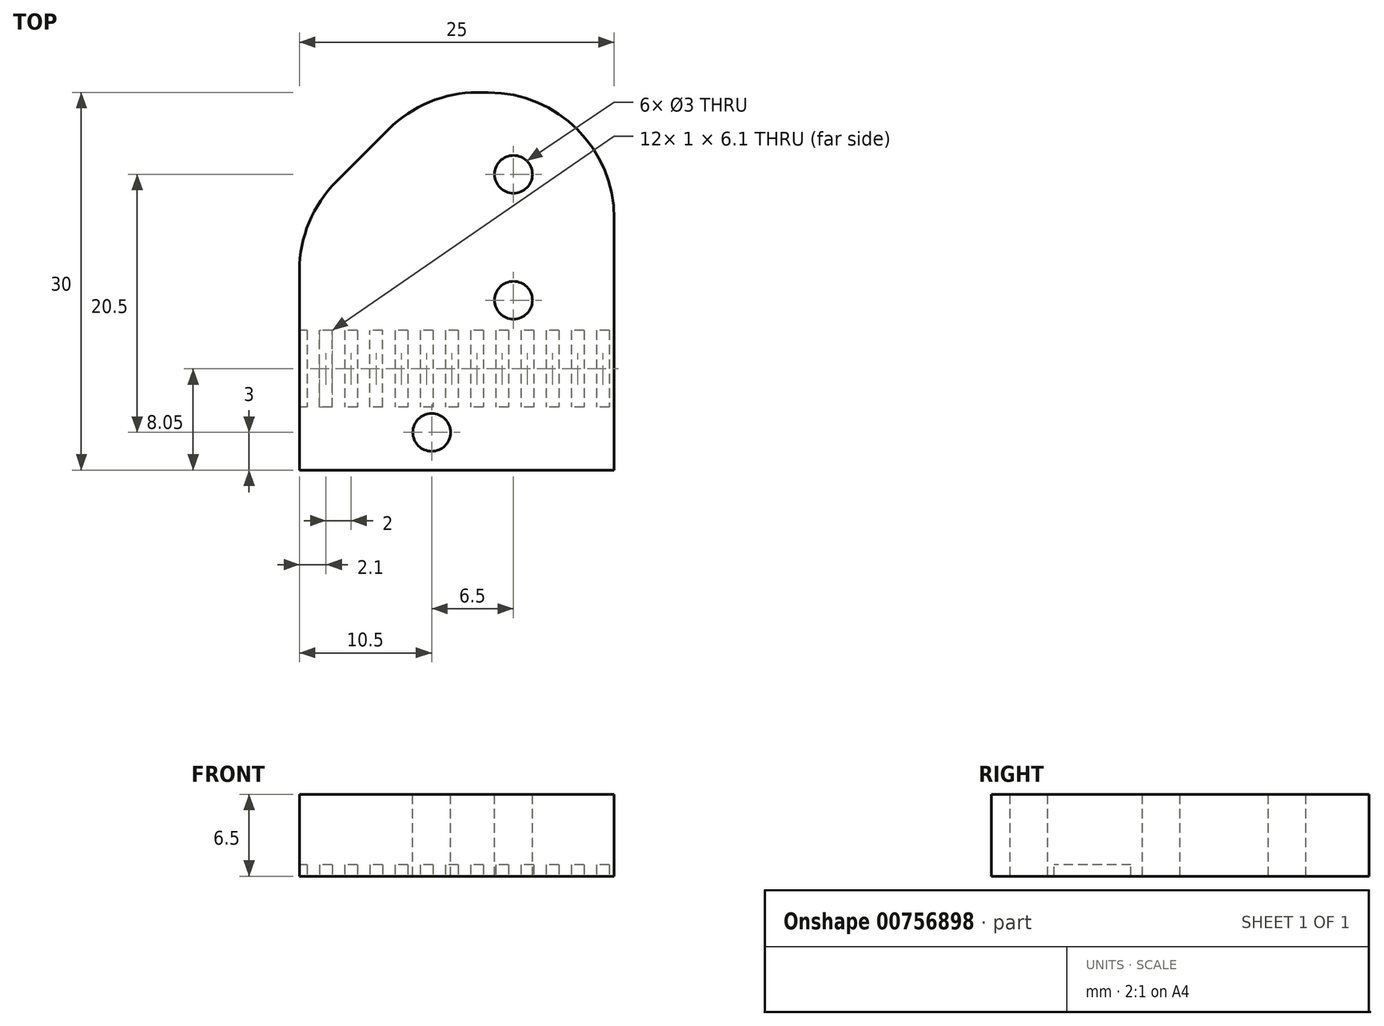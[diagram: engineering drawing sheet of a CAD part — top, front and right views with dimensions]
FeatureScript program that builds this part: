
annotation { "Feature Type Name" : "Feature", "Feature Type Description" : "" }
export const myFeature = defineFeature(function(context is Context, id is Id, definition is map)
    precondition{}
    {
        {
            var Q0;
            Q0=qCreatedBy(makeId("Top.planeOp"),FACE);
            var sketch = newSketch(context, id + "F0", { "sketchPlane" : qUnion([Q0])});
            skLineSegment(sketch, "E0.bottom", {"start": v(12.5, -15) * mm, "end": v(-12.5, -15) * mm});
            skLineSegment(sketch, "E0.top", {"start": v(12.5, 15) * mm, "end": v(-12.5, 15) * mm});
            skLineSegment(sketch, "E0.left", {"start": v(12.5, -15) * mm, "end": v(12.5, 15) * mm});
            skLineSegment(sketch, "E0.right", {"start": v(-12.5, -15) * mm, "end": v(-12.5, 15) * mm});
            skPoint(sketch, "E0.middle", {"position": v(0, 0) * mm});
            skSolve(sketch);
        }
        {
            var Q0;
            Q0=makeQuery(id+"F0.imprint","IMPRINT",FACE,{"disambiguationData":[TD([[makeQuery(id+"F0.imprint","IMPRINT",EDGE,{"derivedFrom":sQuery(id+"F0.wireOp",EDGE,"E0.bottom")}),-1.0]])]});
            extrude(context, id + "F1", {"entities" : qUnion([Q0]), "depth" : 6.5 * mm, "offsetDistance" : 25 * mm});
        }
        {
            var Q0;
            Q0=makeQuery(id+"F1.opExtrude","CAP_FACE",FACE,{"disambiguationData":[OSD([sQuery(id+"F0.wireOp",EDGE,"E0.bottom"),sQuery(id+"F0.wireOp",EDGE,"E0.top"),sQuery(id+"F0.wireOp",EDGE,"E0.left"),sQuery(id+"F0.wireOp",EDGE,"E0.right")])],"isStart":false});
            var sketch = newSketch(context, id + "F2", { "sketchPlane" : qUnion([Q0])});
            skCircle(sketch, "E1", {"center": v(-2, -12) * mm, "radius": 1.5 * mm});
            skPoint(sketch, "E1.centerSnap0", {"position": v(0, -15) * mm});
            skCircle(sketch, "E2", {"center": v(4.5, -1.5) * mm, "radius": 1.5 * mm});
            skCircle(sketch, "E3", {"center": v(4.5, 8.5) * mm, "radius": 1.5 * mm});
            skSolve(sketch);
        }
        {
            var Q0;
            Q0=qSketchRegion(id+"F2",true);
            extrude(context, id + "F3", {"entities" : qUnion([Q0]), "operationType" : NewBodyOperationType.REMOVE, "endBound" : BoundingType.THROUGH_ALL, "oppositeDirection" : true, "depth" : 25 * mm, "offsetDistance" : 25 * mm});
        }
        {
            var Q0;
            {var subQ0=sQuery(id+"F0.wireOp",EDGE,"E0.right");var subQ1=sQuery(id+"F0.wireOp",EDGE,"E0.left");var subQ2=sQuery(id+"F0.wireOp",EDGE,"E0.top");Q0=makeQuery(id+"F5.boolean.opBoolean","SPLIT",FACE,{"disambiguationData":[TD([makeQuery(id+"F1.opExtrude","SWEPT_FACE",FACE,{"disambiguationData":[OSD([subQ2])]})])],"derivedFrom":makeQuery(id+"F1.opExtrude","CAP_FACE",FACE,{"disambiguationData":[OSD([sQuery(id+"F0.wireOp",EDGE,"E0.bottom"),subQ2,subQ1,subQ0])],"isStart":true})});}
            var sketch = newSketch(context, id + "F4", { "sketchPlane" : qUnion([Q0])});
            skLineSegment(sketch, "E4.bottom", {"start": v(12.1, 3.9) * mm, "end": v(11.1, 3.9) * mm});
            skLineSegment(sketch, "E4.top", {"start": v(12.1, 10) * mm, "end": v(11.1, 10) * mm});
            skLineSegment(sketch, "E4.left", {"start": v(12.1, 3.9) * mm, "end": v(12.1, 10) * mm});
            skLineSegment(sketch, "E4.right", {"start": v(11.1, 3.9) * mm, "end": v(11.1, 10) * mm});
            skPoint(sketch, "E4.middle", {"position": v(11.6, 6.95) * mm});
            skLineSegment(sketch, "E5.bottom", {"start": v(10.1, 3.9) * mm, "end": v(9.1, 3.9) * mm});
            skLineSegment(sketch, "E5.top", {"start": v(10.1, 10) * mm, "end": v(9.1, 10) * mm});
            skLineSegment(sketch, "E5.left", {"start": v(10.1, 3.9) * mm, "end": v(10.1, 10) * mm});
            skLineSegment(sketch, "E5.right", {"start": v(9.1, 3.9) * mm, "end": v(9.1, 10) * mm});
            skPoint(sketch, "E5.middle", {"position": v(9.6, 6.95) * mm});
            skLineSegment(sketch, "E6.bottom", {"start": v(8.1, 3.9) * mm, "end": v(7.1, 3.9) * mm});
            skLineSegment(sketch, "E6.top", {"start": v(8.1, 10) * mm, "end": v(7.1, 10) * mm});
            skLineSegment(sketch, "E6.left", {"start": v(8.1, 3.9) * mm, "end": v(8.1, 10) * mm});
            skLineSegment(sketch, "E6.right", {"start": v(7.1, 3.9) * mm, "end": v(7.1, 10) * mm});
            skPoint(sketch, "E6.middle", {"position": v(7.6, 6.95) * mm});
            skLineSegment(sketch, "E7.bottom", {"start": v(6.1, 3.9) * mm, "end": v(5.1, 3.9) * mm});
            skLineSegment(sketch, "E7.top", {"start": v(6.1, 10) * mm, "end": v(5.1, 10) * mm});
            skLineSegment(sketch, "E7.left", {"start": v(6.1, 3.9) * mm, "end": v(6.1, 10) * mm});
            skLineSegment(sketch, "E7.right", {"start": v(5.1, 3.9) * mm, "end": v(5.1, 10) * mm});
            skPoint(sketch, "E7.middle", {"position": v(5.6, 6.95) * mm});
            skLineSegment(sketch, "E8.bottom", {"start": v(4.1, 3.9) * mm, "end": v(3.1, 3.9) * mm});
            skLineSegment(sketch, "E8.top", {"start": v(4.1, 10) * mm, "end": v(3.1, 10) * mm});
            skLineSegment(sketch, "E8.left", {"start": v(4.1, 3.9) * mm, "end": v(4.1, 10) * mm});
            skLineSegment(sketch, "E8.right", {"start": v(3.1, 3.9) * mm, "end": v(3.1, 10) * mm});
            skPoint(sketch, "E8.middle", {"position": v(3.6, 6.95) * mm});
            skLineSegment(sketch, "E9.bottom", {"start": v(2.1, 3.9) * mm, "end": v(1.1, 3.9) * mm});
            skLineSegment(sketch, "E9.top", {"start": v(2.1, 10) * mm, "end": v(1.1, 10) * mm});
            skLineSegment(sketch, "E9.left", {"start": v(2.1, 3.9) * mm, "end": v(2.1, 10) * mm});
            skLineSegment(sketch, "E9.right", {"start": v(1.1, 3.9) * mm, "end": v(1.1, 10) * mm});
            skPoint(sketch, "E9.middle", {"position": v(1.6, 6.95) * mm});
            skLineSegment(sketch, "E10.bottom", {"start": v(0.1, 3.9) * mm, "end": v(-0.9, 3.9) * mm});
            skLineSegment(sketch, "E10.top", {"start": v(0.1, 10) * mm, "end": v(-0.9, 10) * mm});
            skLineSegment(sketch, "E10.left", {"start": v(0.1, 3.9) * mm, "end": v(0.1, 10) * mm});
            skLineSegment(sketch, "E10.right", {"start": v(-0.9, 3.9) * mm, "end": v(-0.9, 10) * mm});
            skPoint(sketch, "E10.middle", {"position": v(-0.4, 6.95) * mm});
            skLineSegment(sketch, "E11", {"start": v(-12.5, 3.9) * mm, "end": v(12.5, 3.9) * mm, "construction": true});
            skLineSegment(sketch, "E12", {"start": v(12.5, 10) * mm, "end": v(-12.5, 10) * mm, "construction": true});
            skLineSegment(sketch, "E13.bottom", {"start": v(-1.9, 3.9) * mm, "end": v(-2.9, 3.9) * mm});
            skLineSegment(sketch, "E13.top", {"start": v(-1.9, 10) * mm, "end": v(-2.9, 10) * mm});
            skLineSegment(sketch, "E13.left", {"start": v(-1.9, 3.9) * mm, "end": v(-1.9, 10) * mm});
            skLineSegment(sketch, "E13.right", {"start": v(-2.9, 3.9) * mm, "end": v(-2.9, 10) * mm});
            skLineSegment(sketch, "E14.bottom", {"start": v(-3.9, 3.9) * mm, "end": v(-4.9, 3.9) * mm});
            skLineSegment(sketch, "E14.top", {"start": v(-3.9, 10) * mm, "end": v(-4.9, 10) * mm});
            skLineSegment(sketch, "E14.left", {"start": v(-3.9, 3.9) * mm, "end": v(-3.9, 10) * mm});
            skLineSegment(sketch, "E14.right", {"start": v(-4.9, 3.9) * mm, "end": v(-4.9, 10) * mm});
            skLineSegment(sketch, "E15.bottom", {"start": v(-5.9, 10) * mm, "end": v(-6.9, 10) * mm});
            skLineSegment(sketch, "E15.top", {"start": v(-5.9, 3.9) * mm, "end": v(-6.9, 3.9) * mm});
            skLineSegment(sketch, "E15.left", {"start": v(-5.9, 10) * mm, "end": v(-5.9, 3.9) * mm});
            skLineSegment(sketch, "E15.right", {"start": v(-6.9, 10) * mm, "end": v(-6.9, 3.9) * mm});
            skLineSegment(sketch, "E16.bottom", {"start": v(-7.9, 3.9) * mm, "end": v(-8.9, 3.9) * mm});
            skLineSegment(sketch, "E16.top", {"start": v(-7.9, 10) * mm, "end": v(-8.9, 10) * mm});
            skLineSegment(sketch, "E16.left", {"start": v(-7.9, 3.9) * mm, "end": v(-7.9, 10) * mm});
            skLineSegment(sketch, "E16.right", {"start": v(-8.9, 3.9) * mm, "end": v(-8.9, 10) * mm});
            skLineSegment(sketch, "E17.bottom", {"start": v(-9.9, 10) * mm, "end": v(-10.9, 10) * mm});
            skLineSegment(sketch, "E17.top", {"start": v(-9.9, 3.9) * mm, "end": v(-10.9, 3.9) * mm});
            skLineSegment(sketch, "E17.left", {"start": v(-9.9, 10) * mm, "end": v(-9.9, 3.9) * mm});
            skLineSegment(sketch, "E17.right", {"start": v(-10.9, 10) * mm, "end": v(-10.9, 3.9) * mm});
            skLineSegment(sketch, "E18.bottom", {"start": v(-11.9, 3.9) * mm, "end": v(-12.9, 3.9) * mm});
            skLineSegment(sketch, "E18.top", {"start": v(-11.9, 10) * mm, "end": v(-12.9, 10) * mm});
            skLineSegment(sketch, "E18.left", {"start": v(-11.9, 3.9) * mm, "end": v(-11.9, 10) * mm});
            skLineSegment(sketch, "E18.right", {"start": v(-12.9, 3.9) * mm, "end": v(-12.9, 10) * mm});
            skSolve(sketch);
        }
        {
            var Q0;
            Q0 = qSketchRegion(id + "F4", true);
            extrude(context, id + "F5", {"entities" : qUnion([Q0]), "operationType" : NewBodyOperationType.REMOVE, "oppositeDirection" : true, "depth" : 0.9 * mm, "offsetDistance" : 25 * mm});
        }
        {
            var Q0;
            Q0=makeQuery(id+"F1.opExtrude","SWEPT_EDGE",EDGE,{"disambiguationData":[OSD([sQuery(id+"F0.wireOp",EDGE,"E0.top"),sQuery(id+"F0.wireOp",EDGE,"E0.right")])]});
            chamfer(context, id + "F6", {"entities" : qUnion([Q0]), "width" : 10 * mm, "tangentPropagation" : true});
        }
        {
            var Q0;
            {var subQ0=sQuery(id+"F0.wireOp",EDGE,"E0.right");Q0=makeQuery(id+"F6.opChamfer","BLEND_EDGE",EDGE,{"blendedFrom":[makeQuery(id+"F1.opExtrude","SWEPT_EDGE",EDGE,{"disambiguationData":[OSD([sQuery(id+"F0.wireOp",EDGE,"E0.top"),subQ0])]}),makeQuery(id+"F1.opExtrude","SWEPT_FACE",FACE,{"disambiguationData":[OSD([subQ0])]})],"blendedInto":[makeQuery(id+"F1.opExtrude","SWEPT_FACE",FACE,{"disambiguationData":[OSD([subQ0])]})]});}
            var Q1;
            {var subQ0=sQuery(id+"F0.wireOp",EDGE,"E0.top");Q1=makeQuery(id+"F6.opChamfer","BLEND_EDGE",EDGE,{"blendedFrom":[makeQuery(id+"F1.opExtrude","SWEPT_EDGE",EDGE,{"disambiguationData":[OSD([subQ0,sQuery(id+"F0.wireOp",EDGE,"E0.right")])]}),makeQuery(id+"F1.opExtrude","SWEPT_FACE",FACE,{"disambiguationData":[OSD([subQ0])]})],"blendedInto":[makeQuery(id+"F1.opExtrude","SWEPT_FACE",FACE,{"disambiguationData":[OSD([subQ0])]})]});}
            var Q2;
            Q2=makeQuery(id+"F1.opExtrude","SWEPT_EDGE",EDGE,{"disambiguationData":[OSD([sQuery(id+"F0.wireOp",EDGE,"E0.top"),sQuery(id+"F0.wireOp",EDGE,"E0.left")])]});
            fillet(context, id + "F7", {"entities" : qUnion([Q0, Q1, Q2]), "radius" : 10 * mm, "tangentPropagation" : true, "allowEdgeOverflow" : false});
        }
    });
